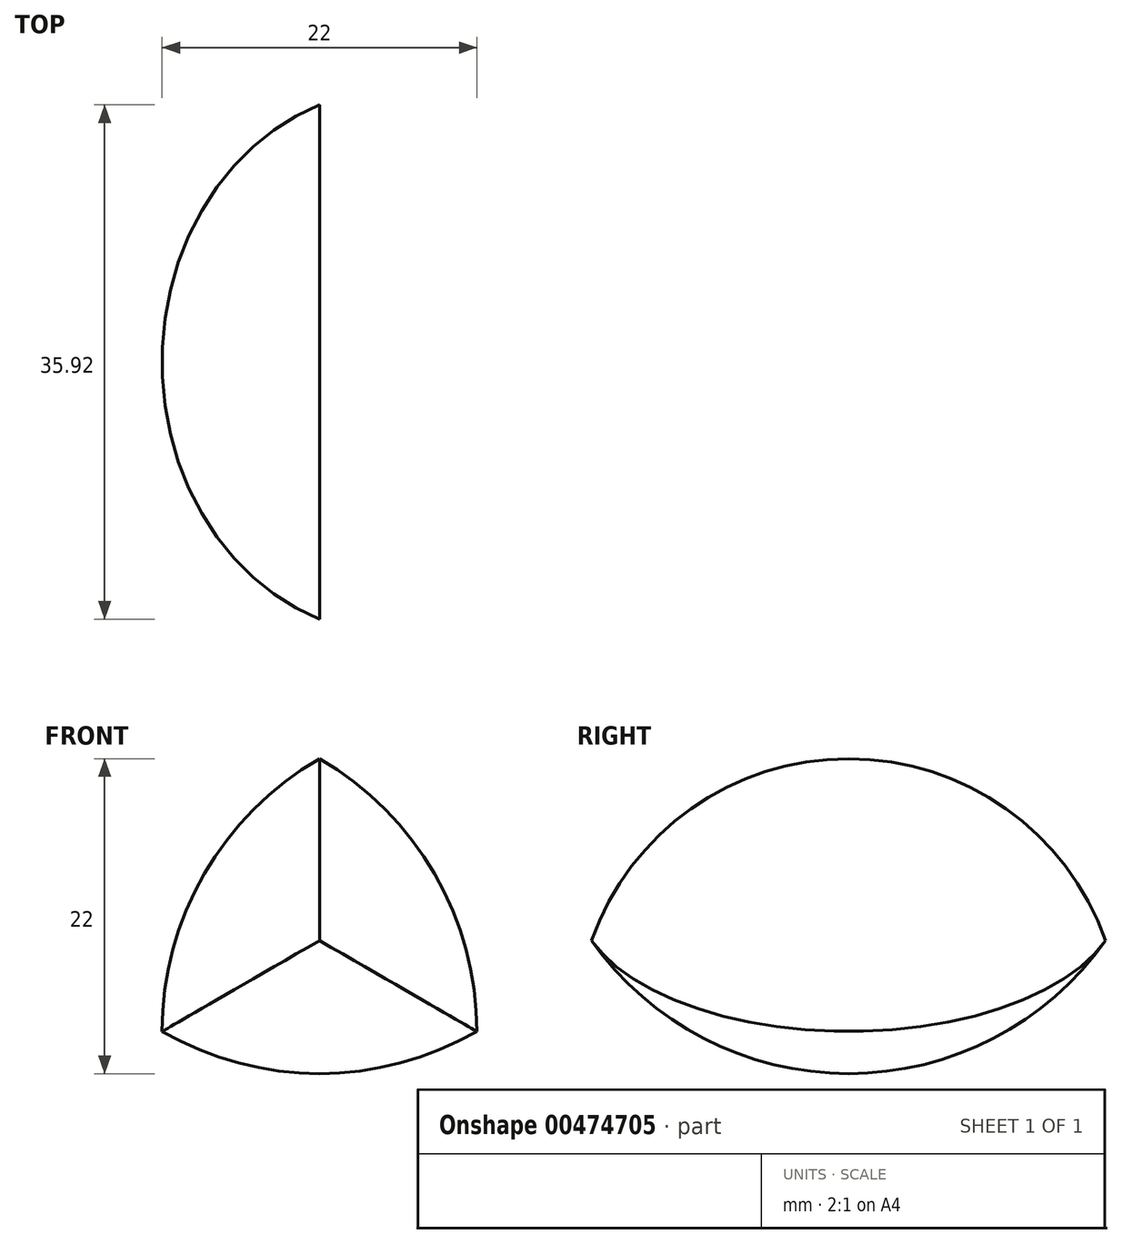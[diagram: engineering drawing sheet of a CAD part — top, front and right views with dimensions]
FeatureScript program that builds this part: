
annotation { "Feature Type Name" : "Feature", "Feature Type Description" : "" }
export const myFeature = defineFeature(function(context is Context, id is Id, definition is map)
    precondition{}
    {
        {
            var Q0;
            Q0=qCreatedBy(makeId("Front.planeOp"),FACE);
            var sketch = newSketch(context, id + "F0", { "sketchPlane" : qUnion([Q0])});
            skCircle(sketch, "E0", {"center": v(0, 0) * mm, "radius": 12.7 * mm, "construction": true});
            skLineSegment(sketch, "E1", {"start": v(-11, -6.35) * mm, "end": v(0, 12.7) * mm, "construction": true});
            skLineSegment(sketch, "E2", {"start": v(0, 12.7) * mm, "end": v(11, -6.35) * mm, "construction": true});
            skLineSegment(sketch, "E3", {"start": v(11, -6.35) * mm, "end": v(-11, -6.35) * mm, "construction": true});
            skArc(sketch, "E4", {"start": v(0, 12.7) * mm, "mid": v(-8.05, 4.65) * mm, "end": v(-11, -6.35) * mm});
            skArc(sketch, "E5", {"start": v(-11, -6.35) * mm, "mid": v(0, -9.3) * mm, "end": v(11, -6.35) * mm});
            skArc(sketch, "E6", {"start": v(0, 12.7) * mm, "mid": v(8.05, 4.65) * mm, "end": v(11, -6.35) * mm});
            skLineSegment(sketch, "E7", {"start": v(11, -6.35) * mm, "end": v(13.76, -1.57) * mm, "construction": true});
            skLineSegment(sketch, "E8", {"start": v(0, 12.7) * mm, "end": v(-5.52, 12.7) * mm, "construction": true});
            skLineSegment(sketch, "E9", {"start": v(-11, -6.35) * mm, "end": v(-8.24, -11.13) * mm, "construction": true});
            skSolve(sketch);
        }
        {
            var Q0;
            Q0=makeQuery(id+"F0.imprint","IMPRINT",FACE,{"disambiguationData":[TD([[makeQuery(id+"F0.imprint","IMPRINT",EDGE,{"derivedFrom":sQuery(id+"F0.wireOp",EDGE,"E4")}),1.0]])]});
            var Q1;
            Q1=sQuery(id+"F0.wireOp",EDGE,"E7");
            revolve(context, id + "F1", {"entities" : qUnion([Q0]), "axis" : qUnion([Q1]), "revolveType" : RevolveType.SYMMETRIC, "angle" : 180 * degree});
        }
        {
            var Q0;
            Q0=makeQuery(id+"F0.imprint","IMPRINT",FACE,{"disambiguationData":[TD([[makeQuery(id+"F0.imprint","IMPRINT",EDGE,{"derivedFrom":sQuery(id+"F0.wireOp",EDGE,"E4")}),1.0]])]});
            var Q1;
            Q1=sQuery(id+"F0.wireOp",EDGE,"E8");
            revolve(context, id + "F2", {"operationType" : NewBodyOperationType.INTERSECT, "entities" : qUnion([Q0]), "axis" : qUnion([Q1]), "revolveType" : RevolveType.SYMMETRIC, "angle" : 180 * degree});
        }
        {
            var Q0;
            Q0=makeQuery(id+"F0.imprint","IMPRINT",FACE,{"disambiguationData":[TD([[makeQuery(id+"F0.imprint","IMPRINT",EDGE,{"derivedFrom":sQuery(id+"F0.wireOp",EDGE,"E4")}),1.0]])]});
            var Q1;
            Q1=sQuery(id+"F0.wireOp",EDGE,"E9");
            revolve(context, id + "F3", {"operationType" : NewBodyOperationType.INTERSECT, "entities" : qUnion([Q0]), "axis" : qUnion([Q1]), "revolveType" : RevolveType.SYMMETRIC, "angle" : 180 * degree});
        }
    });
